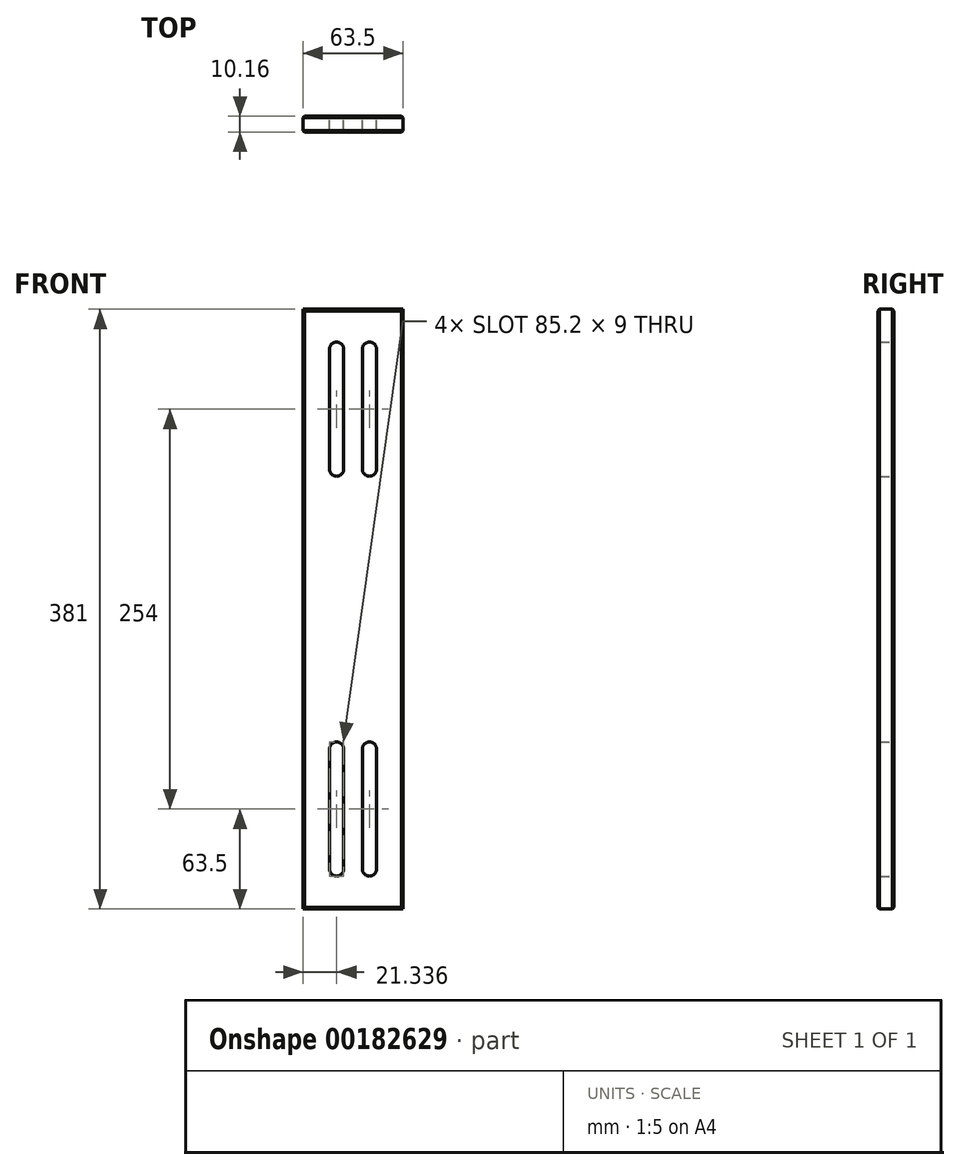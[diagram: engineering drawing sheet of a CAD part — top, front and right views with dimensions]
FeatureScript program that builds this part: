
annotation { "Feature Type Name" : "Feature", "Feature Type Description" : "" }
export const myFeature = defineFeature(function(context is Context, id is Id, definition is map)
    precondition{}
    {
        {
            var Q0;
            Q0=qCreatedBy(makeId("Front.planeOp"),FACE);
            var sketch = newSketch(context, id + "F0", { "sketchPlane" : qUnion([Q0])});
            skLineSegment(sketch, "E0.bottom", {"start": v(31.75, -190.5) * mm, "end": v(-31.75, -190.5) * mm});
            skLineSegment(sketch, "E0.top", {"start": v(31.75, 190.5) * mm, "end": v(-31.75, 190.5) * mm});
            skLineSegment(sketch, "E0.left", {"start": v(31.75, -190.5) * mm, "end": v(31.75, 190.5) * mm});
            skLineSegment(sketch, "E0.right", {"start": v(-31.75, -190.5) * mm, "end": v(-31.75, 190.5) * mm});
            skPoint(sketch, "E0.middle", {"position": v(0, 0) * mm});
            skSolve(sketch);
        }
        {
            var Q0;
            Q0=makeQuery(id+"F0.imprint","IMPRINT",FACE,{"disambiguationData":[TD([[makeQuery(id+"F0.imprint","IMPRINT",EDGE,{"derivedFrom":sQuery(id+"F0.wireOp",EDGE,"E0.bottom")}),-1.0]])]});
            extrude(context, id + "F1", {"entities" : qUnion([Q0]), "depth" : 10.16 * mm});
        }
        {
            var Q0;
            Q0=makeQuery(id+"F1.opExtrude","CAP_FACE",FACE,{"disambiguationData":[OSD([sQuery(id+"F0.wireOp",EDGE,"E0.bottom"),sQuery(id+"F0.wireOp",EDGE,"E0.top"),sQuery(id+"F0.wireOp",EDGE,"E0.left"),sQuery(id+"F0.wireOp",EDGE,"E0.right")])],"isStart":true});
            var sketch = newSketch(context, id + "F2", { "sketchPlane" : qUnion([Q0])});
            skLineSegment(sketch, "E1.bottom", {"start": v(-5.91, -165.1) * mm, "end": v(-14.91, -165.1) * mm});
            skLineSegment(sketch, "E1.top", {"start": v(-5.91, -88.9) * mm, "end": v(-14.91, -88.9) * mm});
            skLineSegment(sketch, "E1.left", {"start": v(-5.91, -165.1) * mm, "end": v(-5.91, -88.9) * mm});
            skLineSegment(sketch, "E1.right", {"start": v(-14.91, -165.1) * mm, "end": v(-14.91, -88.9) * mm});
            skPoint(sketch, "E1.middle", {"position": v(-10.41, -127) * mm});
            skLineSegment(sketch, "E2.bottom", {"start": v(14.91, -165.1) * mm, "end": v(5.91, -165.1) * mm});
            skLineSegment(sketch, "E2.top", {"start": v(14.91, -88.9) * mm, "end": v(5.91, -88.9) * mm});
            skLineSegment(sketch, "E2.left", {"start": v(14.91, -165.1) * mm, "end": v(14.91, -88.9) * mm});
            skLineSegment(sketch, "E2.right", {"start": v(5.91, -165.1) * mm, "end": v(5.91, -88.9) * mm});
            skPoint(sketch, "E2.middle", {"position": v(10.41, -127) * mm});
            skLineSegment(sketch, "E3", {"start": v(31.75, 0) * mm, "end": v(-31.75, 0) * mm});
            skLineSegment(sketch, "E4.MirrorCS", {"start": v(14.91, 88.9) * mm, "end": v(5.91, 88.9) * mm});
            skLineSegment(sketch, "E5.MirrorCS", {"start": v(5.91, 165.1) * mm, "end": v(5.91, 88.9) * mm});
            skLineSegment(sketch, "E6.MirrorCS", {"start": v(14.91, 165.1) * mm, "end": v(14.91, 88.9) * mm});
            skLineSegment(sketch, "E7.MirrorCS", {"start": v(14.91, 165.1) * mm, "end": v(5.91, 165.1) * mm});
            skLineSegment(sketch, "E8.MirrorCS", {"start": v(-14.91, 165.1) * mm, "end": v(-14.91, 88.9) * mm});
            skLineSegment(sketch, "E9.MirrorCS", {"start": v(-5.91, 165.1) * mm, "end": v(-5.91, 88.9) * mm});
            skLineSegment(sketch, "E10.MirrorCS", {"start": v(-5.91, 165.1) * mm, "end": v(-14.91, 165.1) * mm});
            skLineSegment(sketch, "E11.MirrorCS", {"start": v(-5.91, 88.9) * mm, "end": v(-14.91, 88.9) * mm});
            skArc(sketch, "E12", {"start": v(14.91, -88.9) * mm, "mid": v(10.41, -84.4) * mm, "end": v(5.91, -88.9) * mm});
            skArc(sketch, "E13", {"start": v(-5.91, -88.9) * mm, "mid": v(-10.41, -84.4) * mm, "end": v(-14.91, -88.9) * mm});
            skArc(sketch, "E14", {"start": v(-14.91, -165.1) * mm, "mid": v(-10.41, -169.6) * mm, "end": v(-5.91, -165.1) * mm});
            skArc(sketch, "E15", {"start": v(5.91, -165.1) * mm, "mid": v(10.41, -169.6) * mm, "end": v(14.91, -165.1) * mm});
            skArc(sketch, "E16", {"start": v(14.91, 165.1) * mm, "mid": v(10.41, 169.6) * mm, "end": v(5.91, 165.1) * mm});
            skArc(sketch, "E17", {"start": v(-5.91, 165.1) * mm, "mid": v(-10.41, 169.6) * mm, "end": v(-14.91, 165.1) * mm});
            skArc(sketch, "E18", {"start": v(14.91, 88.9) * mm, "mid": v(10.41, 84.4) * mm, "end": v(5.91, 88.9) * mm});
            skArc(sketch, "E19", {"start": v(-5.91, 88.9) * mm, "mid": v(-10.41, 84.4) * mm, "end": v(-14.91, 88.9) * mm});
            skSolve(sketch);
        }
        {
            var Q0;
            Q0=makeQuery(id+"F2.imprint","IMPRINT",FACE,{"disambiguationData":[TD([[makeQuery(id+"F2.imprint","IMPRINT",EDGE,{"derivedFrom":sQuery(id+"F2.wireOp",EDGE,"E1.bottom")}),-1.0]])]});
            var Q1;
            Q1=makeQuery(id+"F2.imprint","IMPRINT",FACE,{"disambiguationData":[TD([[makeQuery(id+"F2.imprint","IMPRINT",EDGE,{"derivedFrom":sQuery(id+"F2.wireOp",EDGE,"E8.MirrorCS")}),1.0]])]});
            var Q2;
            Q2=makeQuery(id+"F2.imprint","IMPRINT",FACE,{"disambiguationData":[TD([[makeQuery(id+"F2.imprint","IMPRINT",EDGE,{"derivedFrom":sQuery(id+"F2.wireOp",EDGE,"E4.MirrorCS")}),-1.0]])]});
            var Q3;
            Q3=makeQuery(id+"F2.imprint","IMPRINT",FACE,{"disambiguationData":[TD([[makeQuery(id+"F2.imprint","IMPRINT",EDGE,{"derivedFrom":sQuery(id+"F2.wireOp",EDGE,"E7.MirrorCS")}),-1.0]])]});
            var Q4;
            Q4=makeQuery(id+"F2.imprint","IMPRINT",FACE,{"disambiguationData":[TD([[makeQuery(id+"F2.imprint","IMPRINT",EDGE,{"derivedFrom":sQuery(id+"F2.wireOp",EDGE,"E10.MirrorCS")}),-1.0]])]});
            var Q5;
            Q5=makeQuery(id+"F2.imprint","IMPRINT",FACE,{"disambiguationData":[TD([[makeQuery(id+"F2.imprint","IMPRINT",EDGE,{"derivedFrom":sQuery(id+"F2.wireOp",EDGE,"E11.MirrorCS")}),1.0]])]});
            var Q6;
            Q6=makeQuery(id+"F2.imprint","IMPRINT",FACE,{"disambiguationData":[TD([[makeQuery(id+"F2.imprint","IMPRINT",EDGE,{"derivedFrom":sQuery(id+"F2.wireOp",EDGE,"E4.MirrorCS")}),1.0]])]});
            var Q7;
            Q7=makeQuery(id+"F2.imprint","IMPRINT",FACE,{"disambiguationData":[TD([[makeQuery(id+"F2.imprint","IMPRINT",EDGE,{"derivedFrom":sQuery(id+"F2.wireOp",EDGE,"E1.top")}),-1.0]])]});
            var Q8;
            Q8=makeQuery(id+"F2.imprint","IMPRINT",FACE,{"disambiguationData":[TD([[makeQuery(id+"F2.imprint","IMPRINT",EDGE,{"derivedFrom":sQuery(id+"F2.wireOp",EDGE,"E2.top")}),-1.0]])]});
            var Q9;
            Q9=makeQuery(id+"F2.imprint","IMPRINT",FACE,{"disambiguationData":[TD([[makeQuery(id+"F2.imprint","IMPRINT",EDGE,{"derivedFrom":sQuery(id+"F2.wireOp",EDGE,"E2.bottom")}),-1.0]])]});
            var Q10;
            Q10=makeQuery(id+"F2.imprint","IMPRINT",FACE,{"disambiguationData":[TD([[makeQuery(id+"F2.imprint","IMPRINT",EDGE,{"derivedFrom":sQuery(id+"F2.wireOp",EDGE,"E2.bottom")}),1.0]])]});
            var Q11;
            Q11=makeQuery(id+"F2.imprint","IMPRINT",FACE,{"disambiguationData":[TD([[makeQuery(id+"F2.imprint","IMPRINT",EDGE,{"derivedFrom":sQuery(id+"F2.wireOp",EDGE,"E1.bottom")}),1.0]])]});
            extrude(context, id + "F3", {"entities" : qUnion([Q0, Q1, Q2, Q3, Q4, Q5, Q6, Q7, Q8, Q9, Q10, Q11]), "operationType" : NewBodyOperationType.REMOVE, "endBound" : BoundingType.THROUGH_ALL, "oppositeDirection" : true, "depth" : 25.4 * mm});
        }
        {
            var Q0;
            Q0=makeQuery(id+"F1.opExtrude","CAP_EDGE",EDGE,{"disambiguationData":[OSD([sQuery(id+"F0.wireOp",EDGE,"E0.right")])],"isStart":false});
            var Q1;
            Q1=makeQuery(id+"F1.opExtrude","CAP_EDGE",EDGE,{"disambiguationData":[OSD([sQuery(id+"F0.wireOp",EDGE,"E0.left")])],"isStart":false});
            var Q2;
            Q2=makeQuery(id+"F1.opExtrude","CAP_EDGE",EDGE,{"disambiguationData":[OSD([sQuery(id+"F0.wireOp",EDGE,"E0.top")])],"isStart":false});
            var Q3;
            Q3=makeQuery(id+"F1.opExtrude","CAP_EDGE",EDGE,{"disambiguationData":[OSD([sQuery(id+"F0.wireOp",EDGE,"E0.bottom")])],"isStart":false});
            var Q4;
            Q4=makeQuery(id+"F1.opExtrude","CAP_EDGE",EDGE,{"disambiguationData":[OSD([sQuery(id+"F0.wireOp",EDGE,"E0.top")])],"isStart":true});
            var Q5;
            Q5=makeQuery(id+"F1.opExtrude","CAP_EDGE",EDGE,{"disambiguationData":[OSD([sQuery(id+"F0.wireOp",EDGE,"E0.right")])],"isStart":true});
            var Q6;
            Q6=makeQuery(id+"F1.opExtrude","CAP_EDGE",EDGE,{"disambiguationData":[OSD([sQuery(id+"F0.wireOp",EDGE,"E0.bottom")])],"isStart":true});
            var Q7;
            Q7=makeQuery(id+"F1.opExtrude","CAP_EDGE",EDGE,{"disambiguationData":[OSD([sQuery(id+"F0.wireOp",EDGE,"E0.left")])],"isStart":true});
            chamfer(context, id + "F4", {"entities" : qUnion([Q0, Q1, Q2, Q3, Q4, Q5, Q6, Q7]), "width" : 1 * mm, "tangentPropagation" : true});
        }
    });
